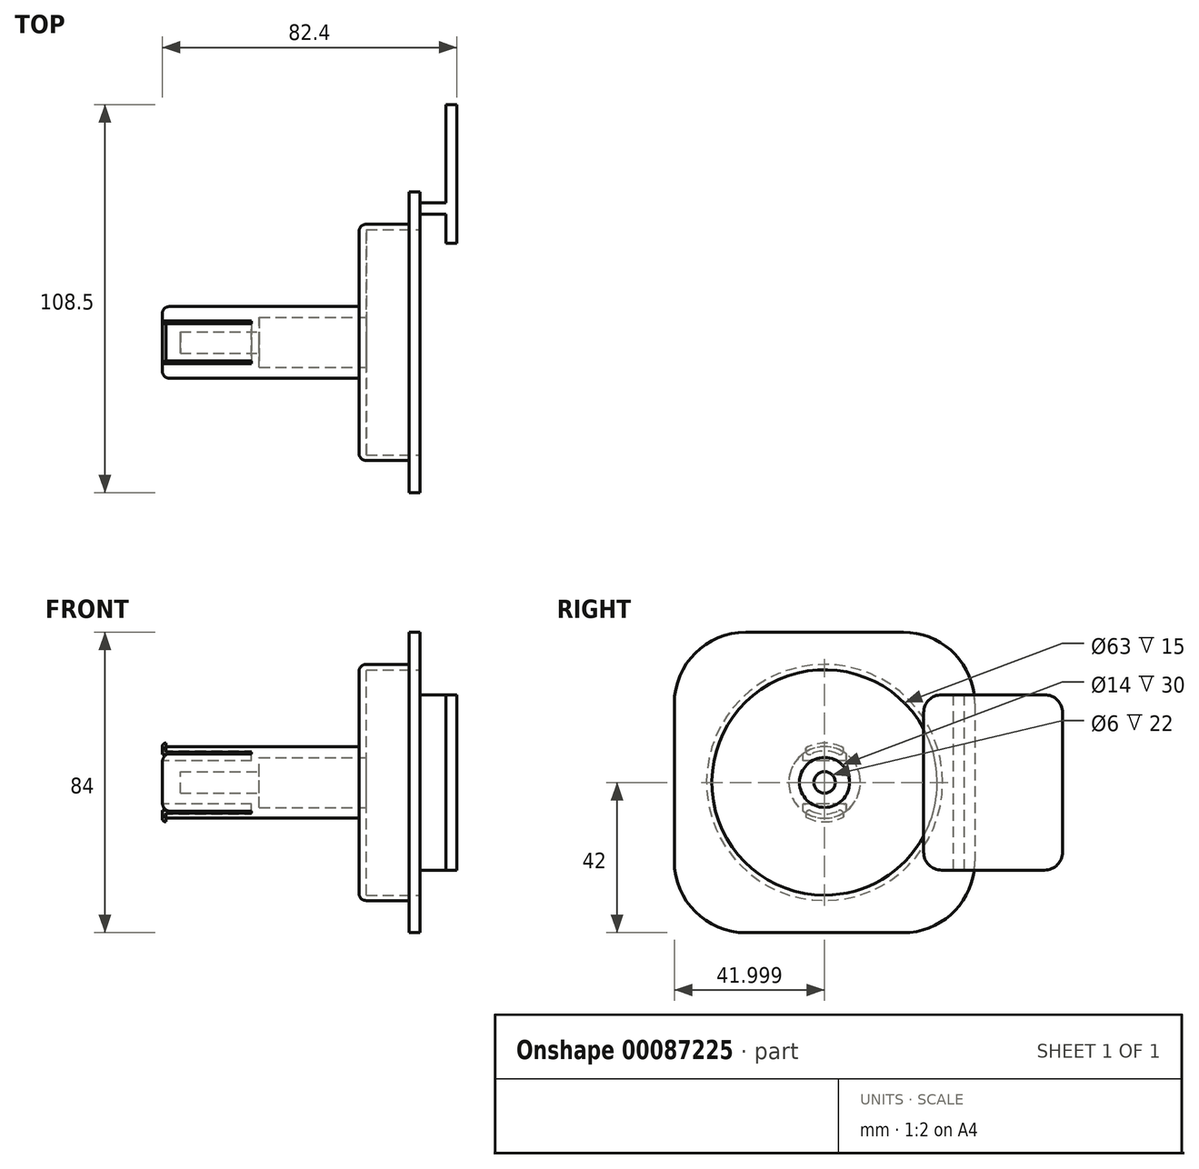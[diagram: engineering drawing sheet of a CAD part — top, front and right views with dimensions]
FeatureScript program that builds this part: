
annotation { "Feature Type Name" : "Feature", "Feature Type Description" : "" }
export const myFeature = defineFeature(function(context is Context, id is Id, definition is map)
    precondition{}
    {
        {
            var Q0;
            Q0=qCreatedBy(makeId("Top.planeOp"),FACE);
            var sketch = newSketch(context, id + "F0", { "sketchPlane" : qUnion([Q0])});
            skLineSegment(sketch, "E0.bottom", {"start": v(21.98, 37.67) * mm, "end": v(18.88, 37.67) * mm});
            skLineSegment(sketch, "E0.top", {"start": v(21.98, -1.13) * mm, "end": v(18.88, -1.13) * mm});
            skLineSegment(sketch, "E0.left", {"start": v(21.98, 37.67) * mm, "end": v(21.98, -1.13) * mm});
            skLineSegment(sketch, "E0.right", {"start": v(18.88, 37.67) * mm, "end": v(18.88, -1.13) * mm});
            skLineSegment(sketch, "E1.bottom", {"start": v(18.88, 10.17) * mm, "end": v(11.68, 10.17) * mm});
            skLineSegment(sketch, "E1.top", {"start": v(18.88, 7.07) * mm, "end": v(11.68, 7.07) * mm});
            skLineSegment(sketch, "E1.left", {"start": v(18.88, 10.17) * mm, "end": v(18.88, 7.07) * mm});
            skLineSegment(sketch, "E1.right", {"start": v(11.68, 10.17) * mm, "end": v(11.68, 7.07) * mm});
            skLineSegment(sketch, "E2.bottom", {"start": v(11.68, 13.17) * mm, "end": v(8.58, 13.17) * mm});
            skLineSegment(sketch, "E2.top", {"start": v(11.68, -70.83) * mm, "end": v(8.58, -70.83) * mm});
            skLineSegment(sketch, "E2.left", {"start": v(11.68, 13.17) * mm, "end": v(11.68, -70.83) * mm});
            skLineSegment(sketch, "E2.right", {"start": v(8.58, 13.17) * mm, "end": v(8.58, -70.83) * mm});
            skSolve(sketch);
        }
        {
            var Q0;
            {var subQ1=sQuery(id+"F0.wireOp",EDGE,"E0.bottom");Q0=makeQuery(id+"F0.imprint","IMPRINT",FACE,{"disambiguationData":[TD([[makeQuery(id+"F0.imprint","IMPRINT",EDGE,{"derivedFrom":subQ1}),1.0]])]});}
            var Q1;
            {var subQ0=sQuery(id+"F0.wireOp",EDGE,"E1.bottom");Q1=makeQuery(id+"F0.imprint","IMPRINT",FACE,{"disambiguationData":[TD([[makeQuery(id+"F0.imprint","IMPRINT",EDGE,{"derivedFrom":subQ0}),1.0]])]});}
            extrude(context, id + "F1", {"entities" : qUnion([Q0, Q1]), "endBound" : BoundingType.SYMMETRIC, "depth" : 49 * mm});
        }
        {
            var Q0;
            {var subQ3=sQuery(id+"F0.wireOp",EDGE,"E2.bottom");Q0=makeQuery(id+"F0.imprint","IMPRINT",FACE,{"disambiguationData":[TD([[makeQuery(id+"F0.imprint","IMPRINT",EDGE,{"derivedFrom":subQ3}),1.0]])]});}
            extrude(context, id + "F2", {"entities" : qUnion([Q0]), "operationType" : NewBodyOperationType.ADD, "endBound" : BoundingType.SYMMETRIC, "depth" : 84 * mm});
        }
        {
            var Q0;
            Q0=makeQuery(id+"F2.opExtrude","SWEPT_FACE",FACE,{"disambiguationData":[OSD([sQuery(id+"F0.wireOp",EDGE,"E2.right")])]});
            var sketch = newSketch(context, id + "F3", { "sketchPlane" : qUnion([Q0])});
            skLineSegment(sketch, "E3", {"start": v(70.83, -42) * mm, "end": v(-13.17, 42) * mm, "construction": true});
            skCircle(sketch, "E4", {"center": v(28.83, 0) * mm, "radius": 33 * mm});
            skSolve(sketch);
        }
        {
            var Q0;
            Q0 = qSketchRegion(id + "F3", true);
            extrude(context, id + "F4", {"entities" : qUnion([Q0]), "operationType" : NewBodyOperationType.ADD, "depth" : 14 * mm});
        }
        {
            var Q0;
            Q0=makeQuery(id+"F4.opExtrude","CAP_FACE",FACE,{"disambiguationData":[OSD([sQuery(id+"F3.wireOp",EDGE,"E4")])],"isStart":false});
            var sketch = newSketch(context, id + "F5", { "sketchPlane" : qUnion([Q0])});
            skCircle(sketch, "E5", {"center": v(28.83, 0) * mm, "radius": 10 * mm});
            skSolve(sketch);
        }
        {
            var Q0;
            Q0=makeQuery(id+"F5.imprint","IMPRINT",FACE,{"disambiguationData":[TD([[makeQuery(id+"F5.imprint","IMPRINT",EDGE,{"derivedFrom":sQuery(id+"F5.wireOp",EDGE,"E5")}),1.0]])]});
            extrude(context, id + "F6", {"entities" : qUnion([Q0]), "operationType" : NewBodyOperationType.ADD, "depth" : 55 * mm});
        }
        {
            var Q0;
            Q0=makeQuery(id+"F6.opExtrude","CAP_FACE",FACE,{"disambiguationData":[OSD([sQuery(id+"F5.wireOp",EDGE,"E5")])],"isStart":false});
            var sketch = newSketch(context, id + "F7", { "sketchPlane" : qUnion([Q0])});
            skLineSegment(sketch, "E6.bottom", {"start": v(22.83, -8) * mm, "end": v(34.83, -8) * mm});
            skLineSegment(sketch, "E6.top", {"start": v(22.83, 8) * mm, "end": v(34.83, 8) * mm});
            skLineSegment(sketch, "E6.left", {"start": v(22.83, -8) * mm, "end": v(22.83, 8) * mm});
            skLineSegment(sketch, "E6.right", {"start": v(34.83, -8) * mm, "end": v(34.83, 8) * mm});
            skLineSegment(sketch, "E7.bottom", {"start": v(22.83, -6) * mm, "end": v(34.83, -6) * mm});
            skLineSegment(sketch, "E7.top", {"start": v(22.83, 6) * mm, "end": v(34.83, 6) * mm});
            skLineSegment(sketch, "E7.left", {"start": v(22.83, -6) * mm, "end": v(22.83, 6) * mm});
            skLineSegment(sketch, "E7.right", {"start": v(34.83, -6) * mm, "end": v(34.83, 6) * mm});
            skSolve(sketch);
        }
        {
            var Q0;
            {var subQ0=sQuery(id+"F7.wireOp",EDGE,"E6.bottom");Q0=makeQuery(id+"F7.imprint","IMPRINT",FACE,{"disambiguationData":[TD([[makeQuery(id+"F7.imprint","IMPRINT",EDGE,{"derivedFrom":subQ0}),1.0]])]});}
            var Q1;
            {var subQ0=sQuery(id+"F7.wireOp",EDGE,"E6.top");Q1=makeQuery(id+"F7.imprint","IMPRINT",FACE,{"disambiguationData":[TD([[makeQuery(id+"F7.imprint","IMPRINT",EDGE,{"derivedFrom":subQ0}),-1.0]])]});}
            var Q2;
            {var subQ0=sQuery(id+"F7.wireOp",EDGE,"E6.bottom");Q2=makeQuery(id+"F7.imprint","IMPRINT",FACE,{"disambiguationData":[TD([[makeQuery(id+"F7.imprint","IMPRINT",EDGE,{"derivedFrom":subQ0}),-1.0]])]});}
            var Q3;
            {var subQ0=sQuery(id+"F7.wireOp",EDGE,"E6.top");Q3=makeQuery(id+"F7.imprint","IMPRINT",FACE,{"disambiguationData":[TD([[makeQuery(id+"F7.imprint","IMPRINT",EDGE,{"derivedFrom":subQ0}),1.0]])]});}
            extrude(context, id + "F8", {"entities" : qUnion([Q0, Q1, Q2, Q3]), "operationType" : NewBodyOperationType.REMOVE, "oppositeDirection" : true, "depth" : 25 * mm});
        }
        {
            var Q0;
            Q0=makeQuery(id+"F8.boolean.opBoolean","COPY",FACE,{"derivedFrom":makeQuery(id+"F8.opExtrude","CAP_FACE",FACE,{"disambiguationData":[OSD([sQuery(id+"F5.wireOp",EDGE,"E5"),sQuery(id+"F7.wireOp",EDGE,"E6.left"),sQuery(id+"F7.wireOp",EDGE,"E6.right"),sQuery(id+"F7.wireOp",EDGE,"E7.bottom")])],"isStart":false})});
            var sketch = newSketch(context, id + "F9", { "sketchPlane" : qUnion([Q0])});
            skArc(sketch, "E8.0", {"start": v(23.55, -7.04) * mm, "mid": v(28.83, -8.8) * mm, "end": v(34.11, -7.04) * mm});
            skLineSegment(sketch, "E9", {"start": v(34.11, -7.04) * mm, "end": v(34.11, -8.5) * mm});
            skLineSegment(sketch, "E10", {"start": v(23.55, -7.04) * mm, "end": v(23.55, -8.5) * mm});
            skSolve(sketch);
        }
        {
            var Q0;
            Q0=makeQuery(id+"F8.boolean.opBoolean","COPY",FACE,{"derivedFrom":makeQuery(id+"F8.opExtrude","CAP_FACE",FACE,{"disambiguationData":[OSD([sQuery(id+"F5.wireOp",EDGE,"E5"),sQuery(id+"F7.wireOp",EDGE,"E6.left"),sQuery(id+"F7.wireOp",EDGE,"E6.right"),sQuery(id+"F7.wireOp",EDGE,"E7.top")])],"isStart":false})});
            var sketch = newSketch(context, id + "F10", { "sketchPlane" : qUnion([Q0])});
            skArc(sketch, "E11.0", {"start": v(34.11, 7.04) * mm, "mid": v(28.83, 8.8) * mm, "end": v(23.55, 7.04) * mm});
            skLineSegment(sketch, "E12", {"start": v(34.11, 7.04) * mm, "end": v(34.11, 8.5) * mm});
            skLineSegment(sketch, "E13", {"start": v(23.55, 7.04) * mm, "end": v(23.55, 8.5) * mm});
            skSolve(sketch);
        }
        {
            var Q0;
            Q0=makeQuery(id+"F9.imprint","IMPRINT",FACE,{"disambiguationData":[TD([[makeQuery(id+"F9.imprint","IMPRINT",EDGE,{"derivedFrom":sQuery(id+"F9.wireOp",EDGE,"E8.0")}),-1.0]])]});
            var Q1;
            Q1=makeQuery(id+"F10.imprint","IMPRINT",FACE,{"disambiguationData":[TD([[makeQuery(id+"F10.imprint","IMPRINT",EDGE,{"derivedFrom":sQuery(id+"F10.wireOp",EDGE,"E11.0")}),-1.0]])]});
            extrude(context, id + "F11", {"entities" : qUnion([Q0, Q1]), "operationType" : NewBodyOperationType.ADD, "depth" : 25 * mm});
        }
        {
            var Q0;
            Q0=makeQuery(id+"F11.opExtrude","CAP_FACE",FACE,{"disambiguationData":[OSD([sQuery(id+"F5.wireOp",EDGE,"E5"),sQuery(id+"F9.wireOp",EDGE,"E8.0"),sQuery(id+"F9.wireOp",EDGE,"E9"),sQuery(id+"F9.wireOp",EDGE,"E10")])],"isStart":false});
            var sketch = newSketch(context, id + "F12", { "sketchPlane" : qUnion([Q0])});
            skLineSegment(sketch, "E14.left", {"start": v(34.11, -8.5) * mm, "end": v(34.11, -9.65) * mm});
            skLineSegment(sketch, "E14.right", {"start": v(23.55, -8.5) * mm, "end": v(23.55, -9.65) * mm});
            skArc(sketch, "E15.0", {"start": v(23.55, -9.65) * mm, "mid": v(28.83, -11) * mm, "end": v(34.11, -9.65) * mm});
            skPoint(sketch, "E16.orphan", {"position": v(23.55, -10.72) * mm});
            skSolve(sketch);
        }
        {
            var Q0;
            Q0=makeQuery(id+"F12.imprint","IMPRINT",FACE,{"disambiguationData":[TD([[makeQuery(id+"F12.imprint","IMPRINT",EDGE,{"derivedFrom":sQuery(id+"F12.wireOp",EDGE,"E14.left")}),-1.0]])]});
            extrude(context, id + "F13", {"entities" : qUnion([Q0]), "operationType" : NewBodyOperationType.ADD, "oppositeDirection" : true, "depth" : 1 * mm});
        }
        {
            var Q0;
            Q0=makeQuery(id+"F11.opExtrude","CAP_FACE",FACE,{"disambiguationData":[OSD([sQuery(id+"F5.wireOp",EDGE,"E5"),sQuery(id+"F10.wireOp",EDGE,"E11.0"),sQuery(id+"F10.wireOp",EDGE,"E12"),sQuery(id+"F10.wireOp",EDGE,"E13")])],"isStart":false});
            var sketch = newSketch(context, id + "F14", { "sketchPlane" : qUnion([Q0])});
            skLineSegment(sketch, "E17.left", {"start": v(34.11, 8.5) * mm, "end": v(34.11, 9.65) * mm});
            skLineSegment(sketch, "E17.right", {"start": v(23.55, 8.5) * mm, "end": v(23.55, 9.65) * mm});
            skArc(sketch, "E18.0", {"start": v(34.11, 9.65) * mm, "mid": v(28.83, 11) * mm, "end": v(23.55, 9.65) * mm});
            skPoint(sketch, "E19.orphan", {"position": v(23.55, 12.07) * mm});
            skSolve(sketch);
        }
        {
            var Q0;
            Q0=makeQuery(id+"F14.imprint","IMPRINT",FACE,{"disambiguationData":[TD([[makeQuery(id+"F14.imprint","IMPRINT",EDGE,{"derivedFrom":sQuery(id+"F14.wireOp",EDGE,"E17.left")}),1.0]])]});
            extrude(context, id + "F15", {"entities" : qUnion([Q0]), "operationType" : NewBodyOperationType.ADD, "oppositeDirection" : true, "depth" : 1 * mm});
        }
        {
            var Q0;
            Q0=makeQuery(id+"F11.opExtrude","SWEPT_EDGE",EDGE,{"disambiguationData":[OSD([sQuery(id+"F10.wireOp",EDGE,"E11.0"),sQuery(id+"F10.wireOp",EDGE,"E12")])]});
            var Q1;
            Q1=makeQuery(id+"F11.opExtrude","SWEPT_EDGE",EDGE,{"disambiguationData":[OSD([sQuery(id+"F10.wireOp",EDGE,"E11.0"),sQuery(id+"F10.wireOp",EDGE,"E13")])]});
            var Q2;
            Q2=makeQuery(id+"F11.opExtrude","SWEPT_EDGE",EDGE,{"disambiguationData":[OSD([sQuery(id+"F9.wireOp",EDGE,"E8.0"),sQuery(id+"F9.wireOp",EDGE,"E9")])]});
            var Q3;
            Q3=makeQuery(id+"F11.opExtrude","SWEPT_EDGE",EDGE,{"disambiguationData":[OSD([sQuery(id+"F9.wireOp",EDGE,"E8.0"),sQuery(id+"F9.wireOp",EDGE,"E10")])]});
            fillet(context, id + "F16", {"entities" : qUnion([Q0, Q1, Q2, Q3]), "radius" : 1 * mm, "tangentPropagation" : true, "allowEdgeOverflow" : false});
        }
        {
            var Q0;
            Q0=makeQuery(id+"F2.opExtrude","SWEPT_FACE",FACE,{"disambiguationData":[OSD([sQuery(id+"F0.wireOp",EDGE,"E2.left")])]});
            var sketch = newSketch(context, id + "F17", { "sketchPlane" : qUnion([Q0])});
            skLineSegment(sketch, "E20", {"start": v(-70.83, 42) * mm, "end": v(13.17, -42) * mm, "construction": true});
            skCircle(sketch, "E21", {"center": v(-28.83, 0) * mm, "radius": 31.5 * mm});
            skSolve(sketch);
        }
        {
            var Q0;
            Q0=makeQuery(id+"F17.imprint","IMPRINT",FACE,{"disambiguationData":[TD([[makeQuery(id+"F17.imprint","IMPRINT",EDGE,{"derivedFrom":sQuery(id+"F17.wireOp",EDGE,"E21")}),1.0]])]});
            extrude(context, id + "F18", {"entities" : qUnion([Q0]), "operationType" : NewBodyOperationType.REMOVE, "oppositeDirection" : true, "depth" : 15 * mm});
        }
        {
            var Q0;
            Q0=makeQuery(id+"F18.boolean.opBoolean","COPY",FACE,{"derivedFrom":makeQuery(id+"F18.opExtrude","CAP_FACE",FACE,{"disambiguationData":[OSD([sQuery(id+"F17.wireOp",EDGE,"E21")])],"isStart":false})});
            var sketch = newSketch(context, id + "F19", { "sketchPlane" : qUnion([Q0])});
            skCircle(sketch, "E22", {"center": v(-28.83, 0) * mm, "radius": 7 * mm});
            skSolve(sketch);
        }
        {
            var Q0;
            Q0=makeQuery(id+"F19.imprint","IMPRINT",FACE,{"disambiguationData":[TD([[makeQuery(id+"F19.imprint","IMPRINT",EDGE,{"derivedFrom":sQuery(id+"F19.wireOp",EDGE,"E22")}),1.0]])]});
            extrude(context, id + "F20", {"entities" : qUnion([Q0]), "operationType" : NewBodyOperationType.REMOVE, "oppositeDirection" : true, "depth" : 30 * mm});
        }
        {
            var Q0;
            Q0=makeQuery(id+"F2.opExtrude","CAP_EDGE",EDGE,{"disambiguationData":[OSD([sQuery(id+"F0.wireOp",EDGE,"E2.bottom")])],"isStart":false});
            var Q1;
            Q1=makeQuery(id+"F2.opExtrude","CAP_EDGE",EDGE,{"disambiguationData":[OSD([sQuery(id+"F0.wireOp",EDGE,"E2.bottom")])],"isStart":true});
            var Q2;
            Q2=makeQuery(id+"F2.opExtrude","CAP_EDGE",EDGE,{"disambiguationData":[OSD([sQuery(id+"F0.wireOp",EDGE,"E2.top")])],"isStart":true});
            var Q3;
            Q3=makeQuery(id+"F2.opExtrude","CAP_EDGE",EDGE,{"disambiguationData":[OSD([sQuery(id+"F0.wireOp",EDGE,"E2.top")])],"isStart":false});
            fillet(context, id + "F21", {"entities" : qUnion([Q0, Q1, Q2, Q3]), "radius" : 20 * mm, "tangentPropagation" : true, "allowEdgeOverflow" : false});
        }
        {
            var Q0;
            Q0=makeQuery(id+"F1.opExtrude","CAP_EDGE",EDGE,{"disambiguationData":[OSD([sQuery(id+"F0.wireOp",EDGE,"E0.bottom")])],"isStart":true});
            var Q1;
            Q1=makeQuery(id+"F1.opExtrude","CAP_EDGE",EDGE,{"disambiguationData":[OSD([sQuery(id+"F0.wireOp",EDGE,"E0.bottom")])],"isStart":false});
            var Q2;
            Q2=makeQuery(id+"F1.opExtrude","CAP_EDGE",EDGE,{"disambiguationData":[OSD([sQuery(id+"F0.wireOp",EDGE,"E0.top")])],"isStart":false});
            var Q3;
            Q3=makeQuery(id+"F1.opExtrude","CAP_EDGE",EDGE,{"disambiguationData":[OSD([sQuery(id+"F0.wireOp",EDGE,"E0.top")])],"isStart":true});
            fillet(context, id + "F22", {"entities" : qUnion([Q0, Q1, Q2, Q3]), "radius" : 5 * mm, "tangentPropagation" : true, "allowEdgeOverflow" : false});
        }
        {
            var Q0;
            Q0=makeQuery(id+"F4.opExtrude","CAP_EDGE",EDGE,{"disambiguationData":[OSD([sQuery(id+"F3.wireOp",EDGE,"E4")])],"isStart":false});
            var Q1;
            {var subQ0=sQuery(id+"F5.wireOp",EDGE,"E5");var subQ1=sQuery(id+"F7.wireOp",EDGE,"E6.right");var subQ2=makeQuery(id+"F6.opExtrude","CAP_EDGE",EDGE,{"disambiguationData":[OSD([subQ0])],"isStart":false});Q1=makeQuery(id+"F8.boolean.opBoolean","SPLIT",EDGE,{"disambiguationData":[TD([makeQuery(id+"F8.opExtrude","SWEPT_FACE",FACE,{"disambiguationData":[OSD([subQ1]),TDD([makeQuery(id+"F7.imprint","IMPRINT",EDGE,{"disambiguationData":[TD([[makeQuery(id+"F7.imprint","INTERSECT",VERTEX,{"derivedFrom":[subQ2,sQuery(id+"F7.wireOp",EDGE,"E6.bottom"),subQ1]}),-1.0]])],"derivedFrom":subQ1})])]})])],"derivedFrom":subQ2});}
            var Q2;
            {var subQ0=sQuery(id+"F5.wireOp",EDGE,"E5");var subQ1=sQuery(id+"F7.wireOp",EDGE,"E6.left");var subQ2=makeQuery(id+"F6.opExtrude","CAP_EDGE",EDGE,{"disambiguationData":[OSD([subQ0])],"isStart":false});Q2=makeQuery(id+"F8.boolean.opBoolean","SPLIT",EDGE,{"disambiguationData":[TD([makeQuery(id+"F8.opExtrude","SWEPT_FACE",FACE,{"disambiguationData":[OSD([subQ1]),TDD([makeQuery(id+"F7.imprint","IMPRINT",EDGE,{"disambiguationData":[TD([[makeQuery(id+"F7.imprint","INTERSECT",VERTEX,{"derivedFrom":[subQ2,sQuery(id+"F7.wireOp",EDGE,"E6.bottom"),subQ1]}),-1.0]])],"derivedFrom":subQ1})])]})])],"derivedFrom":subQ2});}
            fillet(context, id + "F23", {"entities" : qUnion([Q0, Q1, Q2]), "radius" : 2 * mm, "tangentPropagation" : true, "allowEdgeOverflow" : false});
        }
        {
            var Q0;
            Q0=makeQuery(id+"F15.opExtrude","CAP_EDGE",EDGE,{"disambiguationData":[OSD([sQuery(id+"F14.wireOp",EDGE,"E18.0")])],"isStart":true});
            var Q1;
            Q1=makeQuery(id+"F13.opExtrude","CAP_EDGE",EDGE,{"disambiguationData":[OSD([sQuery(id+"F12.wireOp",EDGE,"E15.0")])],"isStart":true});
            fillet(context, id + "F24", {"entities" : qUnion([Q0, Q1]), "radius" : 1 * mm, "tangentPropagation" : true, "allowEdgeOverflow" : false});
        }
        {
            var Q0;
            Q0=makeQuery(id+"F20.boolean.opBoolean","COPY",FACE,{"derivedFrom":makeQuery(id+"F20.opExtrude","CAP_FACE",FACE,{"disambiguationData":[OSD([sQuery(id+"F19.wireOp",EDGE,"E22")])],"isStart":false})});
            var sketch = newSketch(context, id + "F25", { "sketchPlane" : qUnion([Q0])});
            skCircle(sketch, "E23", {"center": v(-28.83, 0) * mm, "radius": 3 * mm});
            skSolve(sketch);
        }
        {
            var Q0;
            Q0=makeQuery(id+"F25.imprint","IMPRINT",FACE,{"disambiguationData":[TD([[makeQuery(id+"F25.imprint","IMPRINT",EDGE,{"derivedFrom":sQuery(id+"F25.wireOp",EDGE,"E23")}),1.0]])]});
            extrude(context, id + "F26", {"entities" : qUnion([Q0]), "operationType" : NewBodyOperationType.REMOVE, "oppositeDirection" : true, "depth" : 22 * mm});
        }
    });
